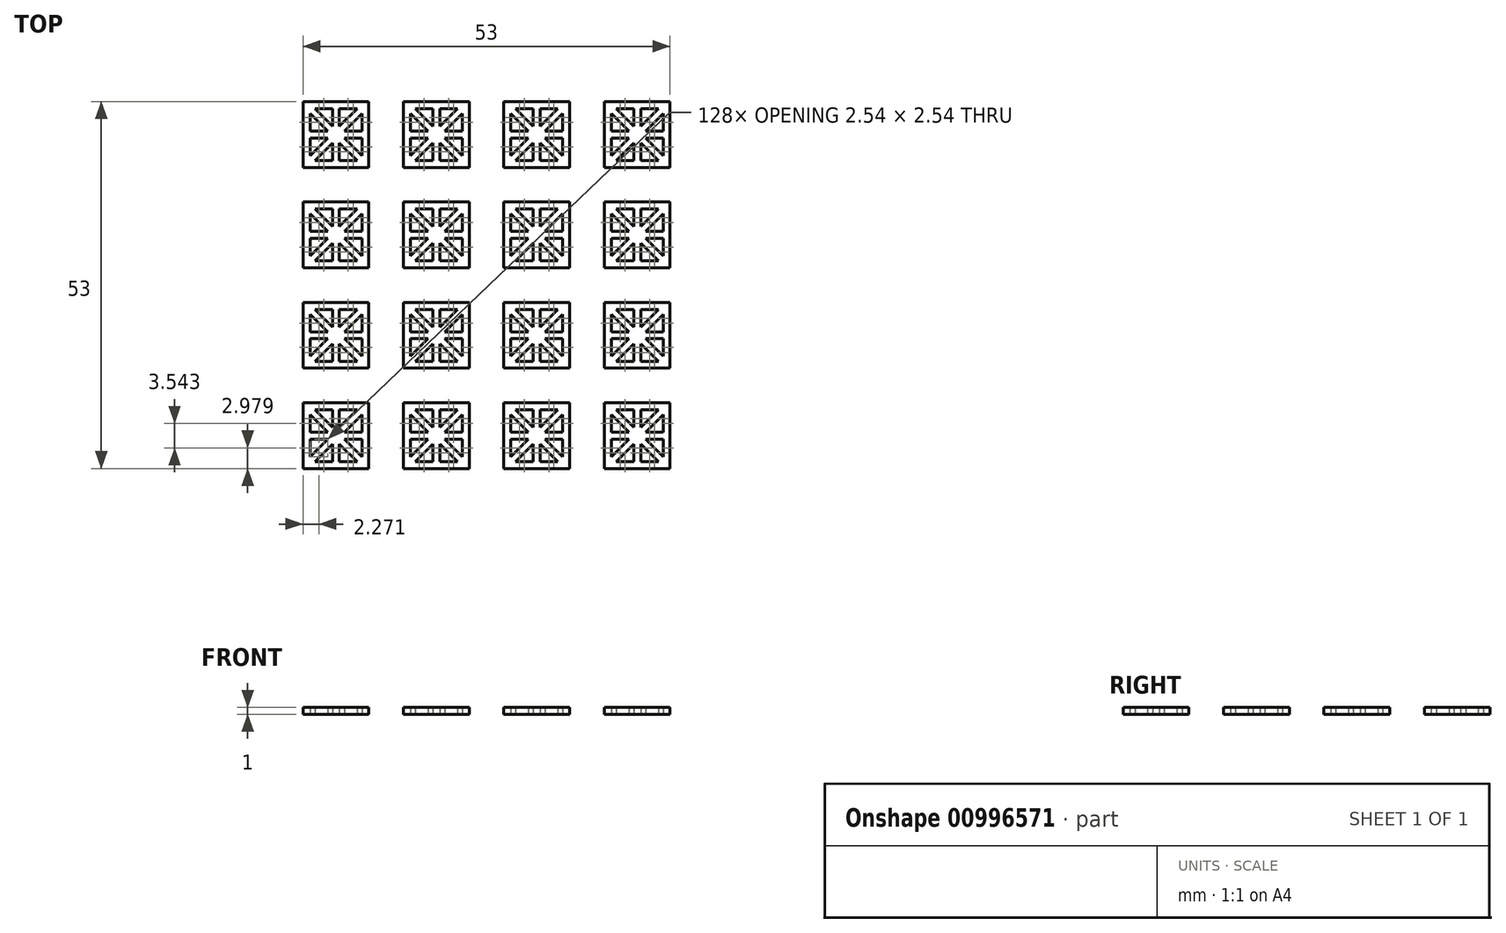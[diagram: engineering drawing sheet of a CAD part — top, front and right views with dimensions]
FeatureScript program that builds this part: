
annotation { "Feature Type Name" : "Feature", "Feature Type Description" : "" }
export const myFeature = defineFeature(function(context is Context, id is Id, definition is map)
    precondition{}
    {
        {
            var Q0;
            Q0=qCreatedBy(makeId("Top.planeOp"),FACE);
            var sketch = newSketch(context, id + "F0", { "sketchPlane" : qUnion([Q0])});
            skLineSegment(sketch, "E0", {"start": v(-0.5, 3.75) * mm, "end": v(-3.04, 3.75) * mm});
            skLineSegment(sketch, "E1", {"start": v(-3.75, 3.04) * mm, "end": v(-3.75, 0.5) * mm});
            skLineSegment(sketch, "E2", {"start": v(-3.04, -3.75) * mm, "end": v(-0.5, -3.75) * mm});
            skLineSegment(sketch, "E3", {"start": v(3.04, 3.75) * mm, "end": v(0.5, 3.75) * mm});
            skPoint(sketch, "E4", {"position": v(0, -4.75) * mm});
            skPoint(sketch, "E5", {"position": v(-4.75, 4.75) * mm});
            skPoint(sketch, "E6", {"position": v(4.75, 4.75) * mm});
            skPoint(sketch, "E7", {"position": v(-4.75, -4.75) * mm});
            skPoint(sketch, "E8", {"position": v(4.75, -4.75) * mm});
            skLineSegment(sketch, "E9", {"start": v(-4.75, 4.75) * mm, "end": v(-4.75, -4.75) * mm});
            skLineSegment(sketch, "E10", {"start": v(4.75, -4.75) * mm, "end": v(-4.75, -4.75) * mm});
            skLineSegment(sketch, "E11", {"start": v(4.75, -4.75) * mm, "end": v(4.75, 4.75) * mm});
            skLineSegment(sketch, "E12", {"start": v(4.75, 4.75) * mm, "end": v(-4.75, 4.75) * mm});
            skPoint(sketch, "E13", {"position": v(-0.5, 3.75) * mm});
            skPoint(sketch, "E14", {"position": v(0.5, 3.75) * mm});
            skPoint(sketch, "E15", {"position": v(-3.75, -0.5) * mm});
            skPoint(sketch, "E16", {"position": v(-3.75, 0.5) * mm});
            skLineSegment(sketch, "E17", {"start": v(-0.5, 3.75) * mm, "end": v(-0.5, 1.2) * mm});
            skLineSegment(sketch, "E18", {"start": v(0.5, 3.75) * mm, "end": v(0.5, 1.2) * mm});
            skLineSegment(sketch, "E19", {"start": v(-3.75, 0.5) * mm, "end": v(-1.2, 0.5) * mm});
            skLineSegment(sketch, "E20", {"start": v(-3.75, -0.5) * mm, "end": v(-1.2, -0.5) * mm});
            skLineSegment(sketch, "E21", {"start": v(-3.75, 3.04) * mm, "end": v(-1.2, 0.5) * mm});
            skLineSegment(sketch, "E22", {"start": v(-3.04, 3.75) * mm, "end": v(-0.5, 1.2) * mm});
            skLineSegment(sketch, "E23", {"start": v(0.5, 1.2) * mm, "end": v(3.04, 3.75) * mm});
            skLineSegment(sketch, "E24", {"start": v(3.04, 3.75) * mm, "end": v(0.5, 1.2) * mm});
            skLineSegment(sketch, "E25", {"start": v(-3.04, -3.75) * mm, "end": v(-0.5, -1.2) * mm});
            skLineSegment(sketch, "E26.trimOffspring", {"start": v(1.2, -0.5) * mm, "end": v(3.75, -3.04) * mm});
            skLineSegment(sketch, "E27.trimOffspring", {"start": v(1.2, 0.5) * mm, "end": v(3.75, 0.5) * mm});
            skLineSegment(sketch, "E28.trimOffspring", {"start": v(1.2, -0.5) * mm, "end": v(3.75, -0.5) * mm});
            skLineSegment(sketch, "E29.trimOffspring", {"start": v(0.5, -1.2) * mm, "end": v(3.04, -3.75) * mm});
            skLineSegment(sketch, "E30.trimOffspring", {"start": v(1.2, 0.5) * mm, "end": v(3.75, 3.04) * mm});
            skLineSegment(sketch, "E31.trimOffspring", {"start": v(-1.2, -0.5) * mm, "end": v(-3.75, -3.04) * mm});
            skLineSegment(sketch, "E32.trimOffspring", {"start": v(0.5, -1.2) * mm, "end": v(0.5, -3.75) * mm});
            skLineSegment(sketch, "E33.trimOffspring", {"start": v(-0.5, -1.2) * mm, "end": v(-0.5, -3.75) * mm});
            skLineSegment(sketch, "E34.trimOffspring", {"start": v(-3.75, -0.5) * mm, "end": v(-3.75, -3.04) * mm});
            skLineSegment(sketch, "E35.trimOffspring", {"start": v(0.5, -3.75) * mm, "end": v(3.04, -3.75) * mm});
            skLineSegment(sketch, "E36.trimOffspring", {"start": v(3.75, 0.5) * mm, "end": v(3.75, 3.04) * mm});
            skLineSegment(sketch, "E37", {"start": v(3.75, -0.5) * mm, "end": v(3.75, -3.04) * mm});
            skPoint(sketch, "E38", {"position": v(9.75, -4.75) * mm});
            skLineSegment(sketch, "E39", {"start": v(14, 3.75) * mm, "end": v(11.46, 3.75) * mm});
            skLineSegment(sketch, "E40", {"start": v(10.75, 3.04) * mm, "end": v(10.75, 0.5) * mm});
            skLineSegment(sketch, "E41", {"start": v(11.46, -3.75) * mm, "end": v(14, -3.75) * mm});
            skLineSegment(sketch, "E42", {"start": v(17.54, 3.75) * mm, "end": v(15, 3.75) * mm});
            skPoint(sketch, "E43", {"position": v(14.5, -4.75) * mm});
            skPoint(sketch, "E44", {"position": v(9.75, 4.75) * mm});
            skPoint(sketch, "E45", {"position": v(19.25, 4.75) * mm});
            skPoint(sketch, "E46", {"position": v(19.25, -4.75) * mm});
            skLineSegment(sketch, "E47", {"start": v(9.75, 4.75) * mm, "end": v(9.75, -4.75) * mm});
            skLineSegment(sketch, "E48", {"start": v(19.25, -4.75) * mm, "end": v(9.75, -4.75) * mm});
            skLineSegment(sketch, "E49", {"start": v(19.25, -4.75) * mm, "end": v(19.25, 4.75) * mm});
            skLineSegment(sketch, "E50", {"start": v(19.25, 4.75) * mm, "end": v(9.75, 4.75) * mm});
            skPoint(sketch, "E51", {"position": v(14, 3.75) * mm});
            skPoint(sketch, "E52", {"position": v(15, 3.75) * mm});
            skPoint(sketch, "E53", {"position": v(10.75, -0.5) * mm});
            skPoint(sketch, "E54", {"position": v(10.75, 0.5) * mm});
            skLineSegment(sketch, "E55", {"start": v(14, 3.75) * mm, "end": v(14, 1.2) * mm});
            skLineSegment(sketch, "E56", {"start": v(15, 3.75) * mm, "end": v(15, 1.2) * mm});
            skLineSegment(sketch, "E57", {"start": v(10.75, 0.5) * mm, "end": v(13.3, 0.5) * mm});
            skLineSegment(sketch, "E58", {"start": v(10.75, -0.5) * mm, "end": v(13.3, -0.5) * mm});
            skLineSegment(sketch, "E59", {"start": v(10.75, 3.04) * mm, "end": v(13.3, 0.5) * mm});
            skLineSegment(sketch, "E60", {"start": v(11.46, 3.75) * mm, "end": v(14, 1.2) * mm});
            skLineSegment(sketch, "E61", {"start": v(15, 1.2) * mm, "end": v(17.54, 3.75) * mm});
            skLineSegment(sketch, "E62", {"start": v(17.54, 3.75) * mm, "end": v(15, 1.2) * mm});
            skLineSegment(sketch, "E63", {"start": v(11.46, -3.75) * mm, "end": v(14, -1.2) * mm});
            skLineSegment(sketch, "E64.trimOffspring", {"start": v(15.7, -0.5) * mm, "end": v(18.25, -3.04) * mm});
            skLineSegment(sketch, "E65.trimOffspring", {"start": v(15.7, 0.5) * mm, "end": v(18.25, 0.5) * mm});
            skLineSegment(sketch, "E66.trimOffspring", {"start": v(15.7, -0.5) * mm, "end": v(18.25, -0.5) * mm});
            skLineSegment(sketch, "E67.trimOffspring", {"start": v(15, -1.2) * mm, "end": v(17.54, -3.75) * mm});
            skLineSegment(sketch, "E68.trimOffspring", {"start": v(15.7, 0.5) * mm, "end": v(18.25, 3.04) * mm});
            skLineSegment(sketch, "E69.trimOffspring", {"start": v(13.3, -0.5) * mm, "end": v(10.75, -3.04) * mm});
            skLineSegment(sketch, "E70.trimOffspring", {"start": v(15, -1.2) * mm, "end": v(15, -3.75) * mm});
            skLineSegment(sketch, "E71.trimOffspring", {"start": v(14, -1.2) * mm, "end": v(14, -3.75) * mm});
            skLineSegment(sketch, "E72.trimOffspring", {"start": v(10.75, -0.5) * mm, "end": v(10.75, -3.04) * mm});
            skLineSegment(sketch, "E73.trimOffspring", {"start": v(15, -3.75) * mm, "end": v(17.54, -3.75) * mm});
            skLineSegment(sketch, "E74.trimOffspring", {"start": v(18.25, 0.5) * mm, "end": v(18.25, 3.04) * mm});
            skLineSegment(sketch, "E75", {"start": v(18.25, -0.5) * mm, "end": v(18.25, -3.04) * mm});
            skPoint(sketch, "E76", {"position": v(24.25, -4.75) * mm});
            skPoint(sketch, "E77", {"position": v(-4.75, 9.75) * mm});
            skPoint(sketch, "E78", {"position": v(9.75, 9.75) * mm});
            skLineSegment(sketch, "E79", {"start": v(28.5, 3.75) * mm, "end": v(25.96, 3.75) * mm});
            skLineSegment(sketch, "E80", {"start": v(25.25, 3.04) * mm, "end": v(25.25, 0.5) * mm});
            skLineSegment(sketch, "E81", {"start": v(25.96, -3.75) * mm, "end": v(28.5, -3.75) * mm});
            skLineSegment(sketch, "E82", {"start": v(32.04, 3.75) * mm, "end": v(29.5, 3.75) * mm});
            skPoint(sketch, "E83", {"position": v(29, -4.75) * mm});
            skPoint(sketch, "E84", {"position": v(24.25, 4.75) * mm});
            skPoint(sketch, "E85", {"position": v(33.75, 4.75) * mm});
            skPoint(sketch, "E86", {"position": v(33.75, -4.75) * mm});
            skLineSegment(sketch, "E87", {"start": v(24.25, 4.75) * mm, "end": v(24.25, -4.75) * mm});
            skLineSegment(sketch, "E88", {"start": v(33.75, -4.75) * mm, "end": v(24.25, -4.75) * mm});
            skLineSegment(sketch, "E89", {"start": v(33.75, -4.75) * mm, "end": v(33.75, 4.75) * mm});
            skLineSegment(sketch, "E90", {"start": v(33.75, 4.75) * mm, "end": v(24.25, 4.75) * mm});
            skPoint(sketch, "E91", {"position": v(28.5, 3.75) * mm});
            skPoint(sketch, "E92", {"position": v(29.5, 3.75) * mm});
            skPoint(sketch, "E93", {"position": v(25.25, -0.5) * mm});
            skPoint(sketch, "E94", {"position": v(25.25, 0.5) * mm});
            skLineSegment(sketch, "E95", {"start": v(28.5, 3.75) * mm, "end": v(28.5, 1.2) * mm});
            skLineSegment(sketch, "E96", {"start": v(29.5, 3.75) * mm, "end": v(29.5, 1.2) * mm});
            skLineSegment(sketch, "E97", {"start": v(25.25, 0.5) * mm, "end": v(27.8, 0.5) * mm});
            skLineSegment(sketch, "E98", {"start": v(25.25, -0.5) * mm, "end": v(27.8, -0.5) * mm});
            skLineSegment(sketch, "E99", {"start": v(25.25, 3.04) * mm, "end": v(27.8, 0.5) * mm});
            skLineSegment(sketch, "E100", {"start": v(25.96, 3.75) * mm, "end": v(28.5, 1.2) * mm});
            skLineSegment(sketch, "E101", {"start": v(29.5, 1.2) * mm, "end": v(32.04, 3.75) * mm});
            skLineSegment(sketch, "E102", {"start": v(32.04, 3.75) * mm, "end": v(29.5, 1.2) * mm});
            skLineSegment(sketch, "E103", {"start": v(25.96, -3.75) * mm, "end": v(28.5, -1.2) * mm});
            skLineSegment(sketch, "E104.trimOffspring", {"start": v(30.2, -0.5) * mm, "end": v(32.75, -3.04) * mm});
            skLineSegment(sketch, "E105.trimOffspring", {"start": v(30.2, 0.5) * mm, "end": v(32.75, 0.5) * mm});
            skLineSegment(sketch, "E106.trimOffspring", {"start": v(30.2, -0.5) * mm, "end": v(32.75, -0.5) * mm});
            skLineSegment(sketch, "E107.trimOffspring", {"start": v(29.5, -1.2) * mm, "end": v(32.04, -3.75) * mm});
            skLineSegment(sketch, "E108.trimOffspring", {"start": v(30.2, 0.5) * mm, "end": v(32.75, 3.04) * mm});
            skLineSegment(sketch, "E109.trimOffspring", {"start": v(27.8, -0.5) * mm, "end": v(25.25, -3.04) * mm});
            skLineSegment(sketch, "E110.trimOffspring", {"start": v(29.5, -1.2) * mm, "end": v(29.5, -3.75) * mm});
            skLineSegment(sketch, "E111.trimOffspring", {"start": v(28.5, -1.2) * mm, "end": v(28.5, -3.75) * mm});
            skLineSegment(sketch, "E112.trimOffspring", {"start": v(25.25, -0.5) * mm, "end": v(25.25, -3.04) * mm});
            skLineSegment(sketch, "E113.trimOffspring", {"start": v(29.5, -3.75) * mm, "end": v(32.04, -3.75) * mm});
            skLineSegment(sketch, "E114.trimOffspring", {"start": v(32.75, 0.5) * mm, "end": v(32.75, 3.04) * mm});
            skLineSegment(sketch, "E115", {"start": v(32.75, -0.5) * mm, "end": v(32.75, -3.04) * mm});
            skLineSegment(sketch, "E116", {"start": v(-0.5, 18.25) * mm, "end": v(-3.04, 18.25) * mm});
            skLineSegment(sketch, "E117", {"start": v(-3.75, 17.54) * mm, "end": v(-3.75, 15) * mm});
            skLineSegment(sketch, "E118", {"start": v(-3.04, 10.75) * mm, "end": v(-0.5, 10.75) * mm});
            skLineSegment(sketch, "E119", {"start": v(3.04, 18.25) * mm, "end": v(0.5, 18.25) * mm});
            skPoint(sketch, "E120", {"position": v(0, 9.75) * mm});
            skPoint(sketch, "E121", {"position": v(-4.75, 19.25) * mm});
            skPoint(sketch, "E122", {"position": v(4.75, 19.25) * mm});
            skPoint(sketch, "E123", {"position": v(4.75, 9.75) * mm});
            skLineSegment(sketch, "E124", {"start": v(-4.75, 19.25) * mm, "end": v(-4.75, 9.75) * mm});
            skLineSegment(sketch, "E125", {"start": v(4.75, 9.75) * mm, "end": v(-4.75, 9.75) * mm});
            skLineSegment(sketch, "E126", {"start": v(4.75, 9.75) * mm, "end": v(4.75, 19.25) * mm});
            skLineSegment(sketch, "E127", {"start": v(4.75, 19.25) * mm, "end": v(-4.75, 19.25) * mm});
            skPoint(sketch, "E128", {"position": v(-0.5, 18.25) * mm});
            skPoint(sketch, "E129", {"position": v(0.5, 18.25) * mm});
            skPoint(sketch, "E130", {"position": v(-3.75, 14) * mm});
            skPoint(sketch, "E131", {"position": v(-3.75, 15) * mm});
            skLineSegment(sketch, "E132", {"start": v(-0.5, 18.25) * mm, "end": v(-0.5, 15.7) * mm});
            skLineSegment(sketch, "E133", {"start": v(0.5, 18.25) * mm, "end": v(0.5, 15.7) * mm});
            skLineSegment(sketch, "E134", {"start": v(-3.75, 15) * mm, "end": v(-1.2, 15) * mm});
            skLineSegment(sketch, "E135", {"start": v(-3.75, 14) * mm, "end": v(-1.2, 14) * mm});
            skLineSegment(sketch, "E136", {"start": v(-3.75, 17.54) * mm, "end": v(-1.2, 15) * mm});
            skLineSegment(sketch, "E137", {"start": v(-3.04, 18.25) * mm, "end": v(-0.5, 15.7) * mm});
            skLineSegment(sketch, "E138", {"start": v(0.5, 15.7) * mm, "end": v(3.04, 18.25) * mm});
            skLineSegment(sketch, "E139", {"start": v(3.04, 18.25) * mm, "end": v(0.5, 15.7) * mm});
            skLineSegment(sketch, "E140", {"start": v(-3.04, 10.75) * mm, "end": v(-0.5, 13.3) * mm});
            skLineSegment(sketch, "E141.trimOffspring", {"start": v(1.2, 14) * mm, "end": v(3.75, 11.46) * mm});
            skLineSegment(sketch, "E142.trimOffspring", {"start": v(1.2, 15) * mm, "end": v(3.75, 15) * mm});
            skLineSegment(sketch, "E143.trimOffspring", {"start": v(1.2, 14) * mm, "end": v(3.75, 14) * mm});
            skLineSegment(sketch, "E144.trimOffspring", {"start": v(0.5, 13.3) * mm, "end": v(3.04, 10.75) * mm});
            skLineSegment(sketch, "E145.trimOffspring", {"start": v(1.2, 15) * mm, "end": v(3.75, 17.54) * mm});
            skLineSegment(sketch, "E146.trimOffspring", {"start": v(-1.2, 14) * mm, "end": v(-3.75, 11.46) * mm});
            skLineSegment(sketch, "E147.trimOffspring", {"start": v(0.5, 13.3) * mm, "end": v(0.5, 10.75) * mm});
            skLineSegment(sketch, "E148.trimOffspring", {"start": v(-0.5, 13.3) * mm, "end": v(-0.5, 10.75) * mm});
            skLineSegment(sketch, "E149.trimOffspring", {"start": v(-3.75, 14) * mm, "end": v(-3.75, 11.46) * mm});
            skLineSegment(sketch, "E150.trimOffspring", {"start": v(0.5, 10.75) * mm, "end": v(3.04, 10.75) * mm});
            skLineSegment(sketch, "E151.trimOffspring", {"start": v(3.75, 15) * mm, "end": v(3.75, 17.54) * mm});
            skLineSegment(sketch, "E152", {"start": v(3.75, 14) * mm, "end": v(3.75, 11.46) * mm});
            skLineSegment(sketch, "E153", {"start": v(14, 18.25) * mm, "end": v(11.46, 18.25) * mm});
            skLineSegment(sketch, "E154", {"start": v(10.75, 17.54) * mm, "end": v(10.75, 15) * mm});
            skLineSegment(sketch, "E155", {"start": v(11.46, 10.75) * mm, "end": v(14, 10.75) * mm});
            skLineSegment(sketch, "E156", {"start": v(17.54, 18.25) * mm, "end": v(15, 18.25) * mm});
            skPoint(sketch, "E157", {"position": v(14.5, 9.75) * mm});
            skPoint(sketch, "E158", {"position": v(9.75, 19.25) * mm});
            skPoint(sketch, "E159", {"position": v(19.25, 19.25) * mm});
            skPoint(sketch, "E160", {"position": v(19.25, 9.75) * mm});
            skLineSegment(sketch, "E161", {"start": v(9.75, 19.25) * mm, "end": v(9.75, 9.75) * mm});
            skLineSegment(sketch, "E162", {"start": v(19.25, 9.75) * mm, "end": v(9.75, 9.75) * mm});
            skLineSegment(sketch, "E163", {"start": v(19.25, 9.75) * mm, "end": v(19.25, 19.25) * mm});
            skLineSegment(sketch, "E164", {"start": v(19.25, 19.25) * mm, "end": v(9.75, 19.25) * mm});
            skPoint(sketch, "E165", {"position": v(14, 18.25) * mm});
            skPoint(sketch, "E166", {"position": v(15, 18.25) * mm});
            skPoint(sketch, "E167", {"position": v(10.75, 14) * mm});
            skPoint(sketch, "E168", {"position": v(10.75, 15) * mm});
            skLineSegment(sketch, "E169", {"start": v(14, 18.25) * mm, "end": v(14, 15.7) * mm});
            skLineSegment(sketch, "E170", {"start": v(15, 18.25) * mm, "end": v(15, 15.7) * mm});
            skLineSegment(sketch, "E171", {"start": v(10.75, 15) * mm, "end": v(13.3, 15) * mm});
            skLineSegment(sketch, "E172", {"start": v(10.75, 14) * mm, "end": v(13.3, 14) * mm});
            skLineSegment(sketch, "E173", {"start": v(10.75, 17.54) * mm, "end": v(13.3, 15) * mm});
            skLineSegment(sketch, "E174", {"start": v(11.46, 18.25) * mm, "end": v(14, 15.7) * mm});
            skLineSegment(sketch, "E175", {"start": v(15, 15.7) * mm, "end": v(17.54, 18.25) * mm});
            skLineSegment(sketch, "E176", {"start": v(17.54, 18.25) * mm, "end": v(15, 15.7) * mm});
            skLineSegment(sketch, "E177", {"start": v(11.46, 10.75) * mm, "end": v(14, 13.3) * mm});
            skLineSegment(sketch, "E178.trimOffspring", {"start": v(15.7, 14) * mm, "end": v(18.25, 11.46) * mm});
            skLineSegment(sketch, "E179.trimOffspring", {"start": v(15.7, 15) * mm, "end": v(18.25, 15) * mm});
            skLineSegment(sketch, "E180.trimOffspring", {"start": v(15.7, 14) * mm, "end": v(18.25, 14) * mm});
            skLineSegment(sketch, "E181.trimOffspring", {"start": v(15, 13.3) * mm, "end": v(17.54, 10.75) * mm});
            skLineSegment(sketch, "E182.trimOffspring", {"start": v(15.7, 15) * mm, "end": v(18.25, 17.54) * mm});
            skLineSegment(sketch, "E183.trimOffspring", {"start": v(13.3, 14) * mm, "end": v(10.75, 11.46) * mm});
            skLineSegment(sketch, "E184.trimOffspring", {"start": v(15, 13.3) * mm, "end": v(15, 10.75) * mm});
            skLineSegment(sketch, "E185.trimOffspring", {"start": v(14, 13.3) * mm, "end": v(14, 10.75) * mm});
            skLineSegment(sketch, "E186.trimOffspring", {"start": v(10.75, 14) * mm, "end": v(10.75, 11.46) * mm});
            skLineSegment(sketch, "E187.trimOffspring", {"start": v(15, 10.75) * mm, "end": v(17.54, 10.75) * mm});
            skLineSegment(sketch, "E188.trimOffspring", {"start": v(18.25, 15) * mm, "end": v(18.25, 17.54) * mm});
            skLineSegment(sketch, "E189", {"start": v(18.25, 14) * mm, "end": v(18.25, 11.46) * mm});
            skLineSegment(sketch, "E190", {"start": v(28.5, 18.25) * mm, "end": v(25.96, 18.25) * mm});
            skLineSegment(sketch, "E191", {"start": v(25.25, 17.54) * mm, "end": v(25.25, 15) * mm});
            skLineSegment(sketch, "E192", {"start": v(25.96, 10.75) * mm, "end": v(28.5, 10.75) * mm});
            skLineSegment(sketch, "E193", {"start": v(32.04, 18.25) * mm, "end": v(29.5, 18.25) * mm});
            skPoint(sketch, "E194", {"position": v(29, 9.75) * mm});
            skPoint(sketch, "E195", {"position": v(24.25, 19.25) * mm});
            skPoint(sketch, "E196", {"position": v(33.75, 19.25) * mm});
            skPoint(sketch, "E197", {"position": v(24.25, 9.75) * mm});
            skPoint(sketch, "E198", {"position": v(33.75, 9.75) * mm});
            skLineSegment(sketch, "E199", {"start": v(24.25, 19.25) * mm, "end": v(24.25, 9.75) * mm});
            skLineSegment(sketch, "E200", {"start": v(33.75, 9.75) * mm, "end": v(24.25, 9.75) * mm});
            skLineSegment(sketch, "E201", {"start": v(33.75, 9.75) * mm, "end": v(33.75, 19.25) * mm});
            skLineSegment(sketch, "E202", {"start": v(33.75, 19.25) * mm, "end": v(24.25, 19.25) * mm});
            skPoint(sketch, "E203", {"position": v(28.5, 18.25) * mm});
            skPoint(sketch, "E204", {"position": v(29.5, 18.25) * mm});
            skPoint(sketch, "E205", {"position": v(25.25, 14) * mm});
            skPoint(sketch, "E206", {"position": v(25.25, 15) * mm});
            skLineSegment(sketch, "E207", {"start": v(28.5, 18.25) * mm, "end": v(28.5, 15.7) * mm});
            skLineSegment(sketch, "E208", {"start": v(29.5, 18.25) * mm, "end": v(29.5, 15.7) * mm});
            skLineSegment(sketch, "E209", {"start": v(25.25, 15) * mm, "end": v(27.8, 15) * mm});
            skLineSegment(sketch, "E210", {"start": v(25.25, 14) * mm, "end": v(27.8, 14) * mm});
            skLineSegment(sketch, "E211", {"start": v(25.25, 17.54) * mm, "end": v(27.8, 15) * mm});
            skLineSegment(sketch, "E212", {"start": v(25.96, 18.25) * mm, "end": v(28.5, 15.7) * mm});
            skLineSegment(sketch, "E213", {"start": v(29.5, 15.7) * mm, "end": v(32.04, 18.25) * mm});
            skLineSegment(sketch, "E214", {"start": v(32.04, 18.25) * mm, "end": v(29.5, 15.7) * mm});
            skLineSegment(sketch, "E215", {"start": v(25.96, 10.75) * mm, "end": v(28.5, 13.3) * mm});
            skLineSegment(sketch, "E216.trimOffspring", {"start": v(30.2, 14) * mm, "end": v(32.75, 11.46) * mm});
            skLineSegment(sketch, "E217.trimOffspring", {"start": v(30.2, 15) * mm, "end": v(32.75, 15) * mm});
            skLineSegment(sketch, "E218.trimOffspring", {"start": v(30.2, 14) * mm, "end": v(32.75, 14) * mm});
            skLineSegment(sketch, "E219.trimOffspring", {"start": v(29.5, 13.3) * mm, "end": v(32.04, 10.75) * mm});
            skLineSegment(sketch, "E220.trimOffspring", {"start": v(30.2, 15) * mm, "end": v(32.75, 17.54) * mm});
            skLineSegment(sketch, "E221.trimOffspring", {"start": v(27.8, 14) * mm, "end": v(25.25, 11.46) * mm});
            skLineSegment(sketch, "E222.trimOffspring", {"start": v(29.5, 13.3) * mm, "end": v(29.5, 10.75) * mm});
            skLineSegment(sketch, "E223.trimOffspring", {"start": v(28.5, 13.3) * mm, "end": v(28.5, 10.75) * mm});
            skLineSegment(sketch, "E224.trimOffspring", {"start": v(25.25, 14) * mm, "end": v(25.25, 11.46) * mm});
            skLineSegment(sketch, "E225.trimOffspring", {"start": v(29.5, 10.75) * mm, "end": v(32.04, 10.75) * mm});
            skLineSegment(sketch, "E226.trimOffspring", {"start": v(32.75, 15) * mm, "end": v(32.75, 17.54) * mm});
            skLineSegment(sketch, "E227", {"start": v(32.75, 14) * mm, "end": v(32.75, 11.46) * mm});
            skPoint(sketch, "E228", {"position": v(38.75, -4.75) * mm});
            skLineSegment(sketch, "E229", {"start": v(43, 3.75) * mm, "end": v(40.46, 3.75) * mm});
            skLineSegment(sketch, "E230", {"start": v(39.75, 3.04) * mm, "end": v(39.75, 0.5) * mm});
            skLineSegment(sketch, "E231", {"start": v(40.46, -3.75) * mm, "end": v(43, -3.75) * mm});
            skLineSegment(sketch, "E232", {"start": v(46.54, 3.75) * mm, "end": v(44, 3.75) * mm});
            skPoint(sketch, "E233", {"position": v(43.5, -4.75) * mm});
            skPoint(sketch, "E234", {"position": v(38.75, 4.75) * mm});
            skPoint(sketch, "E235", {"position": v(48.25, 4.75) * mm});
            skPoint(sketch, "E236", {"position": v(48.25, -4.75) * mm});
            skLineSegment(sketch, "E237", {"start": v(38.75, 4.75) * mm, "end": v(38.75, -4.75) * mm});
            skLineSegment(sketch, "E238", {"start": v(48.25, -4.75) * mm, "end": v(38.75, -4.75) * mm});
            skLineSegment(sketch, "E239", {"start": v(48.25, -4.75) * mm, "end": v(48.25, 4.75) * mm});
            skLineSegment(sketch, "E240", {"start": v(48.25, 4.75) * mm, "end": v(38.75, 4.75) * mm});
            skPoint(sketch, "E241", {"position": v(43, 3.75) * mm});
            skPoint(sketch, "E242", {"position": v(44, 3.75) * mm});
            skPoint(sketch, "E243", {"position": v(39.75, -0.5) * mm});
            skPoint(sketch, "E244", {"position": v(39.75, 0.5) * mm});
            skLineSegment(sketch, "E245", {"start": v(43, 3.75) * mm, "end": v(43, 1.2) * mm});
            skLineSegment(sketch, "E246", {"start": v(44, 3.75) * mm, "end": v(44, 1.2) * mm});
            skLineSegment(sketch, "E247", {"start": v(39.75, 0.5) * mm, "end": v(42.3, 0.5) * mm});
            skLineSegment(sketch, "E248", {"start": v(39.75, -0.5) * mm, "end": v(42.3, -0.5) * mm});
            skLineSegment(sketch, "E249", {"start": v(39.75, 3.04) * mm, "end": v(42.3, 0.5) * mm});
            skLineSegment(sketch, "E250", {"start": v(40.46, 3.75) * mm, "end": v(43, 1.2) * mm});
            skLineSegment(sketch, "E251", {"start": v(44, 1.2) * mm, "end": v(46.54, 3.75) * mm});
            skLineSegment(sketch, "E252", {"start": v(46.54, 3.75) * mm, "end": v(44, 1.2) * mm});
            skLineSegment(sketch, "E253", {"start": v(40.46, -3.75) * mm, "end": v(43, -1.2) * mm});
            skLineSegment(sketch, "E254.trimOffspring", {"start": v(44.7, -0.5) * mm, "end": v(47.25, -3.04) * mm});
            skLineSegment(sketch, "E255.trimOffspring", {"start": v(44.7, 0.5) * mm, "end": v(47.25, 0.5) * mm});
            skLineSegment(sketch, "E256.trimOffspring", {"start": v(44.7, -0.5) * mm, "end": v(47.25, -0.5) * mm});
            skLineSegment(sketch, "E257.trimOffspring", {"start": v(44, -1.2) * mm, "end": v(46.54, -3.75) * mm});
            skLineSegment(sketch, "E258.trimOffspring", {"start": v(44.7, 0.5) * mm, "end": v(47.25, 3.04) * mm});
            skLineSegment(sketch, "E259.trimOffspring", {"start": v(42.3, -0.5) * mm, "end": v(39.75, -3.04) * mm});
            skLineSegment(sketch, "E260.trimOffspring", {"start": v(44, -1.2) * mm, "end": v(44, -3.75) * mm});
            skLineSegment(sketch, "E261.trimOffspring", {"start": v(43, -1.2) * mm, "end": v(43, -3.75) * mm});
            skLineSegment(sketch, "E262.trimOffspring", {"start": v(39.75, -0.5) * mm, "end": v(39.75, -3.04) * mm});
            skLineSegment(sketch, "E263.trimOffspring", {"start": v(44, -3.75) * mm, "end": v(46.54, -3.75) * mm});
            skLineSegment(sketch, "E264.trimOffspring", {"start": v(47.25, 0.5) * mm, "end": v(47.25, 3.04) * mm});
            skLineSegment(sketch, "E265", {"start": v(47.25, -0.5) * mm, "end": v(47.25, -3.04) * mm});
            skLineSegment(sketch, "E266", {"start": v(43, 18.25) * mm, "end": v(40.46, 18.25) * mm});
            skLineSegment(sketch, "E267", {"start": v(39.75, 17.54) * mm, "end": v(39.75, 15) * mm});
            skLineSegment(sketch, "E268", {"start": v(40.46, 10.75) * mm, "end": v(43, 10.75) * mm});
            skLineSegment(sketch, "E269", {"start": v(46.54, 18.25) * mm, "end": v(44, 18.25) * mm});
            skPoint(sketch, "E270", {"position": v(43.5, 9.75) * mm});
            skPoint(sketch, "E271", {"position": v(38.75, 19.25) * mm});
            skPoint(sketch, "E272", {"position": v(48.25, 19.25) * mm});
            skPoint(sketch, "E273", {"position": v(38.75, 9.75) * mm});
            skPoint(sketch, "E274", {"position": v(48.25, 9.75) * mm});
            skLineSegment(sketch, "E275", {"start": v(38.75, 19.25) * mm, "end": v(38.75, 9.75) * mm});
            skLineSegment(sketch, "E276", {"start": v(48.25, 9.75) * mm, "end": v(38.75, 9.75) * mm});
            skLineSegment(sketch, "E277", {"start": v(48.25, 9.75) * mm, "end": v(48.25, 19.25) * mm});
            skLineSegment(sketch, "E278", {"start": v(48.25, 19.25) * mm, "end": v(38.75, 19.25) * mm});
            skPoint(sketch, "E279", {"position": v(43, 18.25) * mm});
            skPoint(sketch, "E280", {"position": v(44, 18.25) * mm});
            skPoint(sketch, "E281", {"position": v(39.75, 14) * mm});
            skPoint(sketch, "E282", {"position": v(39.75, 15) * mm});
            skLineSegment(sketch, "E283", {"start": v(43, 18.25) * mm, "end": v(43, 15.7) * mm});
            skLineSegment(sketch, "E284", {"start": v(44, 18.25) * mm, "end": v(44, 15.7) * mm});
            skLineSegment(sketch, "E285", {"start": v(39.75, 15) * mm, "end": v(42.3, 15) * mm});
            skLineSegment(sketch, "E286", {"start": v(39.75, 14) * mm, "end": v(42.3, 14) * mm});
            skLineSegment(sketch, "E287", {"start": v(39.75, 17.54) * mm, "end": v(42.3, 15) * mm});
            skLineSegment(sketch, "E288", {"start": v(40.46, 18.25) * mm, "end": v(43, 15.7) * mm});
            skLineSegment(sketch, "E289", {"start": v(44, 15.7) * mm, "end": v(46.54, 18.25) * mm});
            skLineSegment(sketch, "E290", {"start": v(46.54, 18.25) * mm, "end": v(44, 15.7) * mm});
            skLineSegment(sketch, "E291", {"start": v(40.46, 10.75) * mm, "end": v(43, 13.3) * mm});
            skLineSegment(sketch, "E292.trimOffspring", {"start": v(44.7, 14) * mm, "end": v(47.25, 11.46) * mm});
            skLineSegment(sketch, "E293.trimOffspring", {"start": v(44.7, 15) * mm, "end": v(47.25, 15) * mm});
            skLineSegment(sketch, "E294.trimOffspring", {"start": v(44.7, 14) * mm, "end": v(47.25, 14) * mm});
            skLineSegment(sketch, "E295.trimOffspring", {"start": v(44, 13.3) * mm, "end": v(46.54, 10.75) * mm});
            skLineSegment(sketch, "E296.trimOffspring", {"start": v(44.7, 15) * mm, "end": v(47.25, 17.54) * mm});
            skLineSegment(sketch, "E297.trimOffspring", {"start": v(42.3, 14) * mm, "end": v(39.75, 11.46) * mm});
            skLineSegment(sketch, "E298.trimOffspring", {"start": v(44, 13.3) * mm, "end": v(44, 10.75) * mm});
            skLineSegment(sketch, "E299.trimOffspring", {"start": v(43, 13.3) * mm, "end": v(43, 10.75) * mm});
            skLineSegment(sketch, "E300.trimOffspring", {"start": v(39.75, 14) * mm, "end": v(39.75, 11.46) * mm});
            skLineSegment(sketch, "E301.trimOffspring", {"start": v(44, 10.75) * mm, "end": v(46.54, 10.75) * mm});
            skLineSegment(sketch, "E302.trimOffspring", {"start": v(47.25, 15) * mm, "end": v(47.25, 17.54) * mm});
            skLineSegment(sketch, "E303", {"start": v(47.25, 14) * mm, "end": v(47.25, 11.46) * mm});
            skPoint(sketch, "E304", {"position": v(-4.75, 24.25) * mm});
            skLineSegment(sketch, "E305", {"start": v(-0.5, 32.75) * mm, "end": v(-3.04, 32.75) * mm});
            skLineSegment(sketch, "E306", {"start": v(-3.75, 32.04) * mm, "end": v(-3.75, 29.5) * mm});
            skLineSegment(sketch, "E307", {"start": v(-3.04, 25.25) * mm, "end": v(-0.5, 25.25) * mm});
            skLineSegment(sketch, "E308", {"start": v(3.04, 32.75) * mm, "end": v(0.5, 32.75) * mm});
            skPoint(sketch, "E309", {"position": v(0, 24.25) * mm});
            skPoint(sketch, "E310", {"position": v(-4.75, 33.75) * mm});
            skPoint(sketch, "E311", {"position": v(4.75, 33.75) * mm});
            skPoint(sketch, "E312", {"position": v(4.75, 24.25) * mm});
            skLineSegment(sketch, "E313", {"start": v(-4.75, 33.75) * mm, "end": v(-4.75, 24.25) * mm});
            skLineSegment(sketch, "E314", {"start": v(4.75, 24.25) * mm, "end": v(-4.75, 24.25) * mm});
            skLineSegment(sketch, "E315", {"start": v(4.75, 24.25) * mm, "end": v(4.75, 33.75) * mm});
            skLineSegment(sketch, "E316", {"start": v(4.75, 33.75) * mm, "end": v(-4.75, 33.75) * mm});
            skPoint(sketch, "E317", {"position": v(-0.5, 32.75) * mm});
            skPoint(sketch, "E318", {"position": v(0.5, 32.75) * mm});
            skPoint(sketch, "E319", {"position": v(-3.75, 28.5) * mm});
            skPoint(sketch, "E320", {"position": v(-3.75, 29.5) * mm});
            skLineSegment(sketch, "E321", {"start": v(-0.5, 32.75) * mm, "end": v(-0.5, 30.2) * mm});
            skLineSegment(sketch, "E322", {"start": v(0.5, 32.75) * mm, "end": v(0.5, 30.2) * mm});
            skLineSegment(sketch, "E323", {"start": v(-3.75, 29.5) * mm, "end": v(-1.2, 29.5) * mm});
            skLineSegment(sketch, "E324", {"start": v(-3.75, 28.5) * mm, "end": v(-1.2, 28.5) * mm});
            skLineSegment(sketch, "E325", {"start": v(-3.75, 32.04) * mm, "end": v(-1.2, 29.5) * mm});
            skLineSegment(sketch, "E326", {"start": v(-3.04, 32.75) * mm, "end": v(-0.5, 30.2) * mm});
            skLineSegment(sketch, "E327", {"start": v(0.5, 30.2) * mm, "end": v(3.04, 32.75) * mm});
            skLineSegment(sketch, "E328", {"start": v(3.04, 32.75) * mm, "end": v(0.5, 30.2) * mm});
            skLineSegment(sketch, "E329", {"start": v(-3.04, 25.25) * mm, "end": v(-0.5, 27.8) * mm});
            skLineSegment(sketch, "E330.trimOffspring", {"start": v(1.2, 28.5) * mm, "end": v(3.75, 25.96) * mm});
            skLineSegment(sketch, "E331.trimOffspring", {"start": v(1.2, 29.5) * mm, "end": v(3.75, 29.5) * mm});
            skLineSegment(sketch, "E332.trimOffspring", {"start": v(1.2, 28.5) * mm, "end": v(3.75, 28.5) * mm});
            skLineSegment(sketch, "E333.trimOffspring", {"start": v(0.5, 27.8) * mm, "end": v(3.04, 25.25) * mm});
            skLineSegment(sketch, "E334.trimOffspring", {"start": v(1.2, 29.5) * mm, "end": v(3.75, 32.04) * mm});
            skLineSegment(sketch, "E335.trimOffspring", {"start": v(-1.2, 28.5) * mm, "end": v(-3.75, 25.96) * mm});
            skLineSegment(sketch, "E336.trimOffspring", {"start": v(0.5, 27.8) * mm, "end": v(0.5, 25.25) * mm});
            skLineSegment(sketch, "E337.trimOffspring", {"start": v(-0.5, 27.8) * mm, "end": v(-0.5, 25.25) * mm});
            skLineSegment(sketch, "E338.trimOffspring", {"start": v(-3.75, 28.5) * mm, "end": v(-3.75, 25.96) * mm});
            skLineSegment(sketch, "E339.trimOffspring", {"start": v(0.5, 25.25) * mm, "end": v(3.04, 25.25) * mm});
            skLineSegment(sketch, "E340.trimOffspring", {"start": v(3.75, 29.5) * mm, "end": v(3.75, 32.04) * mm});
            skLineSegment(sketch, "E341", {"start": v(3.75, 28.5) * mm, "end": v(3.75, 25.96) * mm});
            skPoint(sketch, "E342", {"position": v(9.75, 24.25) * mm});
            skLineSegment(sketch, "E343", {"start": v(14, 32.75) * mm, "end": v(11.46, 32.75) * mm});
            skLineSegment(sketch, "E344", {"start": v(10.75, 32.04) * mm, "end": v(10.75, 29.5) * mm});
            skLineSegment(sketch, "E345", {"start": v(11.46, 25.25) * mm, "end": v(14, 25.25) * mm});
            skLineSegment(sketch, "E346", {"start": v(17.54, 32.75) * mm, "end": v(15, 32.75) * mm});
            skPoint(sketch, "E347", {"position": v(14.5, 24.25) * mm});
            skPoint(sketch, "E348", {"position": v(9.75, 33.75) * mm});
            skPoint(sketch, "E349", {"position": v(19.25, 33.75) * mm});
            skPoint(sketch, "E350", {"position": v(19.25, 24.25) * mm});
            skLineSegment(sketch, "E351", {"start": v(9.75, 33.75) * mm, "end": v(9.75, 24.25) * mm});
            skLineSegment(sketch, "E352", {"start": v(19.25, 24.25) * mm, "end": v(9.75, 24.25) * mm});
            skLineSegment(sketch, "E353", {"start": v(19.25, 24.25) * mm, "end": v(19.25, 33.75) * mm});
            skLineSegment(sketch, "E354", {"start": v(19.25, 33.75) * mm, "end": v(9.75, 33.75) * mm});
            skPoint(sketch, "E355", {"position": v(14, 32.75) * mm});
            skPoint(sketch, "E356", {"position": v(15, 32.75) * mm});
            skPoint(sketch, "E357", {"position": v(10.75, 28.5) * mm});
            skPoint(sketch, "E358", {"position": v(10.75, 29.5) * mm});
            skLineSegment(sketch, "E359", {"start": v(14, 32.75) * mm, "end": v(14, 30.2) * mm});
            skLineSegment(sketch, "E360", {"start": v(15, 32.75) * mm, "end": v(15, 30.2) * mm});
            skLineSegment(sketch, "E361", {"start": v(10.75, 29.5) * mm, "end": v(13.3, 29.5) * mm});
            skLineSegment(sketch, "E362", {"start": v(10.75, 28.5) * mm, "end": v(13.3, 28.5) * mm});
            skLineSegment(sketch, "E363", {"start": v(10.75, 32.04) * mm, "end": v(13.3, 29.5) * mm});
            skLineSegment(sketch, "E364", {"start": v(11.46, 32.75) * mm, "end": v(14, 30.2) * mm});
            skLineSegment(sketch, "E365", {"start": v(15, 30.2) * mm, "end": v(17.54, 32.75) * mm});
            skLineSegment(sketch, "E366", {"start": v(17.54, 32.75) * mm, "end": v(15, 30.2) * mm});
            skLineSegment(sketch, "E367", {"start": v(11.46, 25.25) * mm, "end": v(14, 27.8) * mm});
            skLineSegment(sketch, "E368.trimOffspring", {"start": v(15.7, 28.5) * mm, "end": v(18.25, 25.96) * mm});
            skLineSegment(sketch, "E369.trimOffspring", {"start": v(15.7, 29.5) * mm, "end": v(18.25, 29.5) * mm});
            skLineSegment(sketch, "E370.trimOffspring", {"start": v(15.7, 28.5) * mm, "end": v(18.25, 28.5) * mm});
            skLineSegment(sketch, "E371.trimOffspring", {"start": v(15, 27.8) * mm, "end": v(17.54, 25.25) * mm});
            skLineSegment(sketch, "E372.trimOffspring", {"start": v(15.7, 29.5) * mm, "end": v(18.25, 32.04) * mm});
            skLineSegment(sketch, "E373.trimOffspring", {"start": v(13.3, 28.5) * mm, "end": v(10.75, 25.96) * mm});
            skLineSegment(sketch, "E374.trimOffspring", {"start": v(15, 27.8) * mm, "end": v(15, 25.25) * mm});
            skLineSegment(sketch, "E375.trimOffspring", {"start": v(14, 27.8) * mm, "end": v(14, 25.25) * mm});
            skLineSegment(sketch, "E376.trimOffspring", {"start": v(10.75, 28.5) * mm, "end": v(10.75, 25.96) * mm});
            skLineSegment(sketch, "E377.trimOffspring", {"start": v(15, 25.25) * mm, "end": v(17.54, 25.25) * mm});
            skLineSegment(sketch, "E378.trimOffspring", {"start": v(18.25, 29.5) * mm, "end": v(18.25, 32.04) * mm});
            skLineSegment(sketch, "E379", {"start": v(18.25, 28.5) * mm, "end": v(18.25, 25.96) * mm});
            skPoint(sketch, "E380", {"position": v(24.25, 24.25) * mm});
            skPoint(sketch, "E381", {"position": v(-4.75, 38.75) * mm});
            skPoint(sketch, "E382", {"position": v(9.75, 38.75) * mm});
            skLineSegment(sketch, "E383", {"start": v(28.5, 32.75) * mm, "end": v(25.96, 32.75) * mm});
            skLineSegment(sketch, "E384", {"start": v(25.25, 32.04) * mm, "end": v(25.25, 29.5) * mm});
            skLineSegment(sketch, "E385", {"start": v(25.96, 25.25) * mm, "end": v(28.5, 25.25) * mm});
            skLineSegment(sketch, "E386", {"start": v(32.04, 32.75) * mm, "end": v(29.5, 32.75) * mm});
            skPoint(sketch, "E387", {"position": v(29, 24.25) * mm});
            skPoint(sketch, "E388", {"position": v(24.25, 33.75) * mm});
            skPoint(sketch, "E389", {"position": v(33.75, 33.75) * mm});
            skPoint(sketch, "E390", {"position": v(33.75, 24.25) * mm});
            skLineSegment(sketch, "E391", {"start": v(24.25, 33.75) * mm, "end": v(24.25, 24.25) * mm});
            skLineSegment(sketch, "E392", {"start": v(33.75, 24.25) * mm, "end": v(24.25, 24.25) * mm});
            skLineSegment(sketch, "E393", {"start": v(33.75, 24.25) * mm, "end": v(33.75, 33.75) * mm});
            skLineSegment(sketch, "E394", {"start": v(33.75, 33.75) * mm, "end": v(24.25, 33.75) * mm});
            skPoint(sketch, "E395", {"position": v(28.5, 32.75) * mm});
            skPoint(sketch, "E396", {"position": v(29.5, 32.75) * mm});
            skPoint(sketch, "E397", {"position": v(25.25, 28.5) * mm});
            skPoint(sketch, "E398", {"position": v(25.25, 29.5) * mm});
            skLineSegment(sketch, "E399", {"start": v(28.5, 32.75) * mm, "end": v(28.5, 30.2) * mm});
            skLineSegment(sketch, "E400", {"start": v(29.5, 32.75) * mm, "end": v(29.5, 30.2) * mm});
            skLineSegment(sketch, "E401", {"start": v(25.25, 29.5) * mm, "end": v(27.8, 29.5) * mm});
            skLineSegment(sketch, "E402", {"start": v(25.25, 28.5) * mm, "end": v(27.8, 28.5) * mm});
            skLineSegment(sketch, "E403", {"start": v(25.25, 32.04) * mm, "end": v(27.8, 29.5) * mm});
            skLineSegment(sketch, "E404", {"start": v(25.96, 32.75) * mm, "end": v(28.5, 30.2) * mm});
            skLineSegment(sketch, "E405", {"start": v(29.5, 30.2) * mm, "end": v(32.04, 32.75) * mm});
            skLineSegment(sketch, "E406", {"start": v(32.04, 32.75) * mm, "end": v(29.5, 30.2) * mm});
            skLineSegment(sketch, "E407", {"start": v(25.96, 25.25) * mm, "end": v(28.5, 27.8) * mm});
            skLineSegment(sketch, "E408.trimOffspring", {"start": v(30.2, 28.5) * mm, "end": v(32.75, 25.96) * mm});
            skLineSegment(sketch, "E409.trimOffspring", {"start": v(30.2, 29.5) * mm, "end": v(32.75, 29.5) * mm});
            skLineSegment(sketch, "E410.trimOffspring", {"start": v(30.2, 28.5) * mm, "end": v(32.75, 28.5) * mm});
            skLineSegment(sketch, "E411.trimOffspring", {"start": v(29.5, 27.8) * mm, "end": v(32.04, 25.25) * mm});
            skLineSegment(sketch, "E412.trimOffspring", {"start": v(30.2, 29.5) * mm, "end": v(32.75, 32.04) * mm});
            skLineSegment(sketch, "E413.trimOffspring", {"start": v(27.8, 28.5) * mm, "end": v(25.25, 25.96) * mm});
            skLineSegment(sketch, "E414.trimOffspring", {"start": v(29.5, 27.8) * mm, "end": v(29.5, 25.25) * mm});
            skLineSegment(sketch, "E415.trimOffspring", {"start": v(28.5, 27.8) * mm, "end": v(28.5, 25.25) * mm});
            skLineSegment(sketch, "E416.trimOffspring", {"start": v(25.25, 28.5) * mm, "end": v(25.25, 25.96) * mm});
            skLineSegment(sketch, "E417.trimOffspring", {"start": v(29.5, 25.25) * mm, "end": v(32.04, 25.25) * mm});
            skLineSegment(sketch, "E418.trimOffspring", {"start": v(32.75, 29.5) * mm, "end": v(32.75, 32.04) * mm});
            skLineSegment(sketch, "E419", {"start": v(32.75, 28.5) * mm, "end": v(32.75, 25.96) * mm});
            skLineSegment(sketch, "E420", {"start": v(-0.5, 47.25) * mm, "end": v(-3.04, 47.25) * mm});
            skLineSegment(sketch, "E421", {"start": v(-3.75, 46.54) * mm, "end": v(-3.75, 44) * mm});
            skLineSegment(sketch, "E422", {"start": v(-3.04, 39.75) * mm, "end": v(-0.5, 39.75) * mm});
            skLineSegment(sketch, "E423", {"start": v(3.04, 47.25) * mm, "end": v(0.5, 47.25) * mm});
            skPoint(sketch, "E424", {"position": v(0, 38.75) * mm});
            skPoint(sketch, "E425", {"position": v(-4.75, 48.25) * mm});
            skPoint(sketch, "E426", {"position": v(4.75, 48.25) * mm});
            skPoint(sketch, "E427", {"position": v(4.75, 38.75) * mm});
            skLineSegment(sketch, "E428", {"start": v(-4.75, 48.25) * mm, "end": v(-4.75, 38.75) * mm});
            skLineSegment(sketch, "E429", {"start": v(4.75, 38.75) * mm, "end": v(-4.75, 38.75) * mm});
            skLineSegment(sketch, "E430", {"start": v(4.75, 38.75) * mm, "end": v(4.75, 48.25) * mm});
            skLineSegment(sketch, "E431", {"start": v(4.75, 48.25) * mm, "end": v(-4.75, 48.25) * mm});
            skPoint(sketch, "E432", {"position": v(-0.5, 47.25) * mm});
            skPoint(sketch, "E433", {"position": v(0.5, 47.25) * mm});
            skPoint(sketch, "E434", {"position": v(-3.75, 43) * mm});
            skPoint(sketch, "E435", {"position": v(-3.75, 44) * mm});
            skLineSegment(sketch, "E436", {"start": v(-0.5, 47.25) * mm, "end": v(-0.5, 44.7) * mm});
            skLineSegment(sketch, "E437", {"start": v(0.5, 47.25) * mm, "end": v(0.5, 44.7) * mm});
            skLineSegment(sketch, "E438", {"start": v(-3.75, 44) * mm, "end": v(-1.2, 44) * mm});
            skLineSegment(sketch, "E439", {"start": v(-3.75, 43) * mm, "end": v(-1.2, 43) * mm});
            skLineSegment(sketch, "E440", {"start": v(-3.75, 46.54) * mm, "end": v(-1.2, 44) * mm});
            skLineSegment(sketch, "E441", {"start": v(-3.04, 47.25) * mm, "end": v(-0.5, 44.7) * mm});
            skLineSegment(sketch, "E442", {"start": v(0.5, 44.7) * mm, "end": v(3.04, 47.25) * mm});
            skLineSegment(sketch, "E443", {"start": v(3.04, 47.25) * mm, "end": v(0.5, 44.7) * mm});
            skLineSegment(sketch, "E444", {"start": v(-3.04, 39.75) * mm, "end": v(-0.5, 42.3) * mm});
            skLineSegment(sketch, "E445.trimOffspring", {"start": v(1.2, 43) * mm, "end": v(3.75, 40.46) * mm});
            skLineSegment(sketch, "E446.trimOffspring", {"start": v(1.2, 44) * mm, "end": v(3.75, 44) * mm});
            skLineSegment(sketch, "E447.trimOffspring", {"start": v(1.2, 43) * mm, "end": v(3.75, 43) * mm});
            skLineSegment(sketch, "E448.trimOffspring", {"start": v(0.5, 42.3) * mm, "end": v(3.04, 39.75) * mm});
            skLineSegment(sketch, "E449.trimOffspring", {"start": v(1.2, 44) * mm, "end": v(3.75, 46.54) * mm});
            skLineSegment(sketch, "E450.trimOffspring", {"start": v(-1.2, 43) * mm, "end": v(-3.75, 40.46) * mm});
            skLineSegment(sketch, "E451.trimOffspring", {"start": v(0.5, 42.3) * mm, "end": v(0.5, 39.75) * mm});
            skLineSegment(sketch, "E452.trimOffspring", {"start": v(-0.5, 42.3) * mm, "end": v(-0.5, 39.75) * mm});
            skLineSegment(sketch, "E453.trimOffspring", {"start": v(-3.75, 43) * mm, "end": v(-3.75, 40.46) * mm});
            skLineSegment(sketch, "E454.trimOffspring", {"start": v(0.5, 39.75) * mm, "end": v(3.04, 39.75) * mm});
            skLineSegment(sketch, "E455.trimOffspring", {"start": v(3.75, 44) * mm, "end": v(3.75, 46.54) * mm});
            skLineSegment(sketch, "E456", {"start": v(3.75, 43) * mm, "end": v(3.75, 40.46) * mm});
            skLineSegment(sketch, "E457", {"start": v(14, 47.25) * mm, "end": v(11.46, 47.25) * mm});
            skLineSegment(sketch, "E458", {"start": v(10.75, 46.54) * mm, "end": v(10.75, 44) * mm});
            skLineSegment(sketch, "E459", {"start": v(11.46, 39.75) * mm, "end": v(14, 39.75) * mm});
            skLineSegment(sketch, "E460", {"start": v(17.54, 47.25) * mm, "end": v(15, 47.25) * mm});
            skPoint(sketch, "E461", {"position": v(14.5, 38.75) * mm});
            skPoint(sketch, "E462", {"position": v(9.75, 48.25) * mm});
            skPoint(sketch, "E463", {"position": v(19.25, 48.25) * mm});
            skPoint(sketch, "E464", {"position": v(19.25, 38.75) * mm});
            skLineSegment(sketch, "E465", {"start": v(9.75, 48.25) * mm, "end": v(9.75, 38.75) * mm});
            skLineSegment(sketch, "E466", {"start": v(19.25, 38.75) * mm, "end": v(9.75, 38.75) * mm});
            skLineSegment(sketch, "E467", {"start": v(19.25, 38.75) * mm, "end": v(19.25, 48.25) * mm});
            skLineSegment(sketch, "E468", {"start": v(19.25, 48.25) * mm, "end": v(9.75, 48.25) * mm});
            skPoint(sketch, "E469", {"position": v(14, 47.25) * mm});
            skPoint(sketch, "E470", {"position": v(15, 47.25) * mm});
            skPoint(sketch, "E471", {"position": v(10.75, 43) * mm});
            skPoint(sketch, "E472", {"position": v(10.75, 44) * mm});
            skLineSegment(sketch, "E473", {"start": v(14, 47.25) * mm, "end": v(14, 44.7) * mm});
            skLineSegment(sketch, "E474", {"start": v(15, 47.25) * mm, "end": v(15, 44.7) * mm});
            skLineSegment(sketch, "E475", {"start": v(10.75, 44) * mm, "end": v(13.3, 44) * mm});
            skLineSegment(sketch, "E476", {"start": v(10.75, 43) * mm, "end": v(13.3, 43) * mm});
            skLineSegment(sketch, "E477", {"start": v(10.75, 46.54) * mm, "end": v(13.3, 44) * mm});
            skLineSegment(sketch, "E478", {"start": v(11.46, 47.25) * mm, "end": v(14, 44.7) * mm});
            skLineSegment(sketch, "E479", {"start": v(15, 44.7) * mm, "end": v(17.54, 47.25) * mm});
            skLineSegment(sketch, "E480", {"start": v(17.54, 47.25) * mm, "end": v(15, 44.7) * mm});
            skLineSegment(sketch, "E481", {"start": v(11.46, 39.75) * mm, "end": v(14, 42.3) * mm});
            skLineSegment(sketch, "E482.trimOffspring", {"start": v(15.7, 43) * mm, "end": v(18.25, 40.46) * mm});
            skLineSegment(sketch, "E483.trimOffspring", {"start": v(15.7, 44) * mm, "end": v(18.25, 44) * mm});
            skLineSegment(sketch, "E484.trimOffspring", {"start": v(15.7, 43) * mm, "end": v(18.25, 43) * mm});
            skLineSegment(sketch, "E485.trimOffspring", {"start": v(15, 42.3) * mm, "end": v(17.54, 39.75) * mm});
            skLineSegment(sketch, "E486.trimOffspring", {"start": v(15.7, 44) * mm, "end": v(18.25, 46.54) * mm});
            skLineSegment(sketch, "E487.trimOffspring", {"start": v(13.3, 43) * mm, "end": v(10.75, 40.46) * mm});
            skLineSegment(sketch, "E488.trimOffspring", {"start": v(15, 42.3) * mm, "end": v(15, 39.75) * mm});
            skLineSegment(sketch, "E489.trimOffspring", {"start": v(14, 42.3) * mm, "end": v(14, 39.75) * mm});
            skLineSegment(sketch, "E490.trimOffspring", {"start": v(10.75, 43) * mm, "end": v(10.75, 40.46) * mm});
            skLineSegment(sketch, "E491.trimOffspring", {"start": v(15, 39.75) * mm, "end": v(17.54, 39.75) * mm});
            skLineSegment(sketch, "E492.trimOffspring", {"start": v(18.25, 44) * mm, "end": v(18.25, 46.54) * mm});
            skLineSegment(sketch, "E493", {"start": v(18.25, 43) * mm, "end": v(18.25, 40.46) * mm});
            skLineSegment(sketch, "E494", {"start": v(28.5, 47.25) * mm, "end": v(25.96, 47.25) * mm});
            skLineSegment(sketch, "E495", {"start": v(25.25, 46.54) * mm, "end": v(25.25, 44) * mm});
            skLineSegment(sketch, "E496", {"start": v(25.96, 39.75) * mm, "end": v(28.5, 39.75) * mm});
            skLineSegment(sketch, "E497", {"start": v(32.04, 47.25) * mm, "end": v(29.5, 47.25) * mm});
            skPoint(sketch, "E498", {"position": v(29, 38.75) * mm});
            skPoint(sketch, "E499", {"position": v(24.25, 48.25) * mm});
            skPoint(sketch, "E500", {"position": v(33.75, 48.25) * mm});
            skPoint(sketch, "E501", {"position": v(24.25, 38.75) * mm});
            skPoint(sketch, "E502", {"position": v(33.75, 38.75) * mm});
            skLineSegment(sketch, "E503", {"start": v(24.25, 48.25) * mm, "end": v(24.25, 38.75) * mm});
            skLineSegment(sketch, "E504", {"start": v(33.75, 38.75) * mm, "end": v(24.25, 38.75) * mm});
            skLineSegment(sketch, "E505", {"start": v(33.75, 38.75) * mm, "end": v(33.75, 48.25) * mm});
            skLineSegment(sketch, "E506", {"start": v(33.75, 48.25) * mm, "end": v(24.25, 48.25) * mm});
            skPoint(sketch, "E507", {"position": v(28.5, 47.25) * mm});
            skPoint(sketch, "E508", {"position": v(29.5, 47.25) * mm});
            skPoint(sketch, "E509", {"position": v(25.25, 43) * mm});
            skPoint(sketch, "E510", {"position": v(25.25, 44) * mm});
            skLineSegment(sketch, "E511", {"start": v(28.5, 47.25) * mm, "end": v(28.5, 44.7) * mm});
            skLineSegment(sketch, "E512", {"start": v(29.5, 47.25) * mm, "end": v(29.5, 44.7) * mm});
            skLineSegment(sketch, "E513", {"start": v(25.25, 44) * mm, "end": v(27.8, 44) * mm});
            skLineSegment(sketch, "E514", {"start": v(25.25, 43) * mm, "end": v(27.8, 43) * mm});
            skLineSegment(sketch, "E515", {"start": v(25.25, 46.54) * mm, "end": v(27.8, 44) * mm});
            skLineSegment(sketch, "E516", {"start": v(25.96, 47.25) * mm, "end": v(28.5, 44.7) * mm});
            skLineSegment(sketch, "E517", {"start": v(29.5, 44.7) * mm, "end": v(32.04, 47.25) * mm});
            skLineSegment(sketch, "E518", {"start": v(32.04, 47.25) * mm, "end": v(29.5, 44.7) * mm});
            skLineSegment(sketch, "E519", {"start": v(25.96, 39.75) * mm, "end": v(28.5, 42.3) * mm});
            skLineSegment(sketch, "E520.trimOffspring", {"start": v(30.2, 43) * mm, "end": v(32.75, 40.46) * mm});
            skLineSegment(sketch, "E521.trimOffspring", {"start": v(30.2, 44) * mm, "end": v(32.75, 44) * mm});
            skLineSegment(sketch, "E522.trimOffspring", {"start": v(30.2, 43) * mm, "end": v(32.75, 43) * mm});
            skLineSegment(sketch, "E523.trimOffspring", {"start": v(29.5, 42.3) * mm, "end": v(32.04, 39.75) * mm});
            skLineSegment(sketch, "E524.trimOffspring", {"start": v(30.2, 44) * mm, "end": v(32.75, 46.54) * mm});
            skLineSegment(sketch, "E525.trimOffspring", {"start": v(27.8, 43) * mm, "end": v(25.25, 40.46) * mm});
            skLineSegment(sketch, "E526.trimOffspring", {"start": v(29.5, 42.3) * mm, "end": v(29.5, 39.75) * mm});
            skLineSegment(sketch, "E527.trimOffspring", {"start": v(28.5, 42.3) * mm, "end": v(28.5, 39.75) * mm});
            skLineSegment(sketch, "E528.trimOffspring", {"start": v(25.25, 43) * mm, "end": v(25.25, 40.46) * mm});
            skLineSegment(sketch, "E529.trimOffspring", {"start": v(29.5, 39.75) * mm, "end": v(32.04, 39.75) * mm});
            skLineSegment(sketch, "E530.trimOffspring", {"start": v(32.75, 44) * mm, "end": v(32.75, 46.54) * mm});
            skLineSegment(sketch, "E531", {"start": v(32.75, 43) * mm, "end": v(32.75, 40.46) * mm});
            skPoint(sketch, "E532", {"position": v(38.75, 24.25) * mm});
            skLineSegment(sketch, "E533", {"start": v(43, 32.75) * mm, "end": v(40.46, 32.75) * mm});
            skLineSegment(sketch, "E534", {"start": v(39.75, 32.04) * mm, "end": v(39.75, 29.5) * mm});
            skLineSegment(sketch, "E535", {"start": v(40.46, 25.25) * mm, "end": v(43, 25.25) * mm});
            skLineSegment(sketch, "E536", {"start": v(46.54, 32.75) * mm, "end": v(44, 32.75) * mm});
            skPoint(sketch, "E537", {"position": v(43.5, 24.25) * mm});
            skPoint(sketch, "E538", {"position": v(38.75, 33.75) * mm});
            skPoint(sketch, "E539", {"position": v(48.25, 33.75) * mm});
            skPoint(sketch, "E540", {"position": v(48.25, 24.25) * mm});
            skLineSegment(sketch, "E541", {"start": v(38.75, 33.75) * mm, "end": v(38.75, 24.25) * mm});
            skLineSegment(sketch, "E542", {"start": v(48.25, 24.25) * mm, "end": v(38.75, 24.25) * mm});
            skLineSegment(sketch, "E543", {"start": v(48.25, 24.25) * mm, "end": v(48.25, 33.75) * mm});
            skLineSegment(sketch, "E544", {"start": v(48.25, 33.75) * mm, "end": v(38.75, 33.75) * mm});
            skPoint(sketch, "E545", {"position": v(43, 32.75) * mm});
            skPoint(sketch, "E546", {"position": v(44, 32.75) * mm});
            skPoint(sketch, "E547", {"position": v(39.75, 28.5) * mm});
            skPoint(sketch, "E548", {"position": v(39.75, 29.5) * mm});
            skLineSegment(sketch, "E549", {"start": v(43, 32.75) * mm, "end": v(43, 30.2) * mm});
            skLineSegment(sketch, "E550", {"start": v(44, 32.75) * mm, "end": v(44, 30.2) * mm});
            skLineSegment(sketch, "E551", {"start": v(39.75, 29.5) * mm, "end": v(42.3, 29.5) * mm});
            skLineSegment(sketch, "E552", {"start": v(39.75, 28.5) * mm, "end": v(42.3, 28.5) * mm});
            skLineSegment(sketch, "E553", {"start": v(39.75, 32.04) * mm, "end": v(42.3, 29.5) * mm});
            skLineSegment(sketch, "E554", {"start": v(40.46, 32.75) * mm, "end": v(43, 30.2) * mm});
            skLineSegment(sketch, "E555", {"start": v(44, 30.2) * mm, "end": v(46.54, 32.75) * mm});
            skLineSegment(sketch, "E556", {"start": v(46.54, 32.75) * mm, "end": v(44, 30.2) * mm});
            skLineSegment(sketch, "E557", {"start": v(40.46, 25.25) * mm, "end": v(43, 27.8) * mm});
            skLineSegment(sketch, "E558.trimOffspring", {"start": v(44.7, 28.5) * mm, "end": v(47.25, 25.96) * mm});
            skLineSegment(sketch, "E559.trimOffspring", {"start": v(44.7, 29.5) * mm, "end": v(47.25, 29.5) * mm});
            skLineSegment(sketch, "E560.trimOffspring", {"start": v(44.7, 28.5) * mm, "end": v(47.25, 28.5) * mm});
            skLineSegment(sketch, "E561.trimOffspring", {"start": v(44, 27.8) * mm, "end": v(46.54, 25.25) * mm});
            skLineSegment(sketch, "E562.trimOffspring", {"start": v(44.7, 29.5) * mm, "end": v(47.25, 32.04) * mm});
            skLineSegment(sketch, "E563.trimOffspring", {"start": v(42.3, 28.5) * mm, "end": v(39.75, 25.96) * mm});
            skLineSegment(sketch, "E564.trimOffspring", {"start": v(44, 27.8) * mm, "end": v(44, 25.25) * mm});
            skLineSegment(sketch, "E565.trimOffspring", {"start": v(43, 27.8) * mm, "end": v(43, 25.25) * mm});
            skLineSegment(sketch, "E566.trimOffspring", {"start": v(39.75, 28.5) * mm, "end": v(39.75, 25.96) * mm});
            skLineSegment(sketch, "E567.trimOffspring", {"start": v(44, 25.25) * mm, "end": v(46.54, 25.25) * mm});
            skLineSegment(sketch, "E568.trimOffspring", {"start": v(47.25, 29.5) * mm, "end": v(47.25, 32.04) * mm});
            skLineSegment(sketch, "E569", {"start": v(47.25, 28.5) * mm, "end": v(47.25, 25.96) * mm});
            skLineSegment(sketch, "E570", {"start": v(43, 47.25) * mm, "end": v(40.46, 47.25) * mm});
            skLineSegment(sketch, "E571", {"start": v(39.75, 46.54) * mm, "end": v(39.75, 44) * mm});
            skLineSegment(sketch, "E572", {"start": v(40.46, 39.75) * mm, "end": v(43, 39.75) * mm});
            skLineSegment(sketch, "E573", {"start": v(46.54, 47.25) * mm, "end": v(44, 47.25) * mm});
            skPoint(sketch, "E574", {"position": v(43.5, 38.75) * mm});
            skPoint(sketch, "E575", {"position": v(38.75, 48.25) * mm});
            skPoint(sketch, "E576", {"position": v(48.25, 48.25) * mm});
            skPoint(sketch, "E577", {"position": v(38.75, 38.75) * mm});
            skPoint(sketch, "E578", {"position": v(48.25, 38.75) * mm});
            skLineSegment(sketch, "E579", {"start": v(38.75, 48.25) * mm, "end": v(38.75, 38.75) * mm});
            skLineSegment(sketch, "E580", {"start": v(48.25, 38.75) * mm, "end": v(38.75, 38.75) * mm});
            skLineSegment(sketch, "E581", {"start": v(48.25, 38.75) * mm, "end": v(48.25, 48.25) * mm});
            skLineSegment(sketch, "E582", {"start": v(48.25, 48.25) * mm, "end": v(38.75, 48.25) * mm});
            skPoint(sketch, "E583", {"position": v(43, 47.25) * mm});
            skPoint(sketch, "E584", {"position": v(44, 47.25) * mm});
            skPoint(sketch, "E585", {"position": v(39.75, 43) * mm});
            skPoint(sketch, "E586", {"position": v(39.75, 44) * mm});
            skLineSegment(sketch, "E587", {"start": v(43, 47.25) * mm, "end": v(43, 44.7) * mm});
            skLineSegment(sketch, "E588", {"start": v(44, 47.25) * mm, "end": v(44, 44.7) * mm});
            skLineSegment(sketch, "E589", {"start": v(39.75, 44) * mm, "end": v(42.3, 44) * mm});
            skLineSegment(sketch, "E590", {"start": v(39.75, 43) * mm, "end": v(42.3, 43) * mm});
            skLineSegment(sketch, "E591", {"start": v(39.75, 46.54) * mm, "end": v(42.3, 44) * mm});
            skLineSegment(sketch, "E592", {"start": v(40.46, 47.25) * mm, "end": v(43, 44.7) * mm});
            skLineSegment(sketch, "E593", {"start": v(44, 44.7) * mm, "end": v(46.54, 47.25) * mm});
            skLineSegment(sketch, "E594", {"start": v(46.54, 47.25) * mm, "end": v(44, 44.7) * mm});
            skLineSegment(sketch, "E595", {"start": v(40.46, 39.75) * mm, "end": v(43, 42.3) * mm});
            skLineSegment(sketch, "E596.trimOffspring", {"start": v(44.7, 43) * mm, "end": v(47.25, 40.46) * mm});
            skLineSegment(sketch, "E597.trimOffspring", {"start": v(44.7, 44) * mm, "end": v(47.25, 44) * mm});
            skLineSegment(sketch, "E598.trimOffspring", {"start": v(44.7, 43) * mm, "end": v(47.25, 43) * mm});
            skLineSegment(sketch, "E599.trimOffspring", {"start": v(44, 42.3) * mm, "end": v(46.54, 39.75) * mm});
            skLineSegment(sketch, "E600.trimOffspring", {"start": v(44.7, 44) * mm, "end": v(47.25, 46.54) * mm});
            skLineSegment(sketch, "E601.trimOffspring", {"start": v(42.3, 43) * mm, "end": v(39.75, 40.46) * mm});
            skLineSegment(sketch, "E602.trimOffspring", {"start": v(44, 42.3) * mm, "end": v(44, 39.75) * mm});
            skLineSegment(sketch, "E603.trimOffspring", {"start": v(43, 42.3) * mm, "end": v(43, 39.75) * mm});
            skLineSegment(sketch, "E604.trimOffspring", {"start": v(39.75, 43) * mm, "end": v(39.75, 40.46) * mm});
            skLineSegment(sketch, "E605.trimOffspring", {"start": v(44, 39.75) * mm, "end": v(46.54, 39.75) * mm});
            skLineSegment(sketch, "E606.trimOffspring", {"start": v(47.25, 44) * mm, "end": v(47.25, 46.54) * mm});
            skLineSegment(sketch, "E607", {"start": v(47.25, 43) * mm, "end": v(47.25, 40.46) * mm});
            skSolve(sketch);
        }
        {
            var Q0;
            Q0 = qSketchRegion(id + "F0", true);
            extrude(context, id + "F1", {"entities" : qUnion([Q0]), "depth" : 1 * mm, "offsetDistance" : 25 * mm});
        }
        {
            var Q0;
            Q0=makeQuery(id+"F1.opExtrude","SWEPT_FACE",FACE,{"disambiguationData":[OSD([sQuery(id+"F0.wireOp",EDGE,"E582")])]});
            cPlane(context, id + "F2", {"entities" : qUnion([Q0]), "cplaneType" : CPlaneType.OFFSET, "offset" : 4.75 * mm, "oppositeDirection" : true, "width" : 150 * mm, "height" : 150 * mm});
        }
    });
